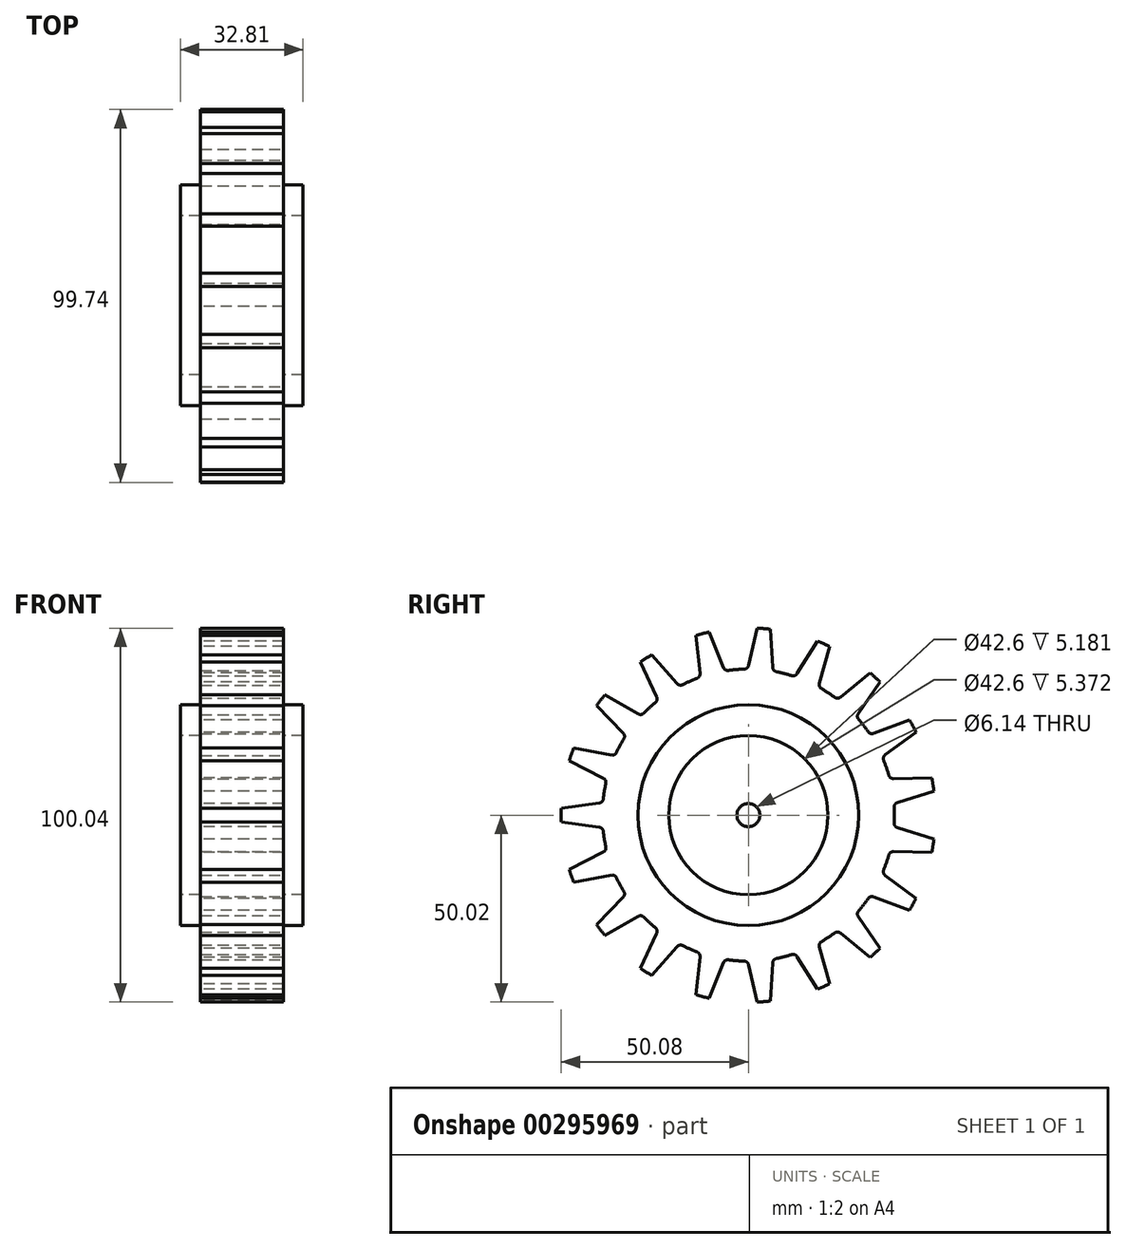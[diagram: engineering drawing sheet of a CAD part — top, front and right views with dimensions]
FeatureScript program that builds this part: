
annotation { "Feature Type Name" : "Feature", "Feature Type Description" : "" }
export const myFeature = defineFeature(function(context is Context, id is Id, definition is map)
    precondition{}
    {
        {
            var Q0;
            Q0=qCreatedBy(makeId("Top.planeOp"),FACE);
            var sketch = newSketch(context, id + "F0", { "sketchPlane" : qUnion([Q0])});
            skLineSegment(sketch, "E0.top", {"start": v(-11.7, 3.07) * mm, "end": v(10.55, 3.07) * mm});
            skLineSegment(sketch, "E0.left", {"start": v(-11.7, 21.68) * mm, "end": v(-11.7, 3.07) * mm});
            skLineSegment(sketch, "E0.right", {"start": v(10.55, 21.68) * mm, "end": v(10.55, 3.07) * mm});
            skLineSegment(sketch, "E1.bottom", {"start": v(-17.08, 29.55) * mm, "end": v(-11.7, 29.55) * mm});
            skLineSegment(sketch, "E1.top", {"start": v(-17.08, 21.3) * mm, "end": v(-11.7, 21.3) * mm});
            skLineSegment(sketch, "E1.left", {"start": v(-17.08, 29.55) * mm, "end": v(-17.08, 21.3) * mm});
            skLineSegment(sketch, "E1.right", {"start": v(15.73, 29.55) * mm, "end": v(15.73, 21.3) * mm});
            skLineSegment(sketch, "E2.top", {"start": v(-11.7, 50.08) * mm, "end": v(10.55, 50.08) * mm});
            skLineSegment(sketch, "E2.left", {"start": v(-11.7, 29.55) * mm, "end": v(-11.7, 50.08) * mm});
            skLineSegment(sketch, "E2.right", {"start": v(10.55, 29.55) * mm, "end": v(10.55, 50.08) * mm});
            skLineSegment(sketch, "E3.trimOffspring", {"start": v(10.55, 21.3) * mm, "end": v(15.73, 21.3) * mm});
            skLineSegment(sketch, "E4.trimOffspring", {"start": v(10.55, 29.55) * mm, "end": v(15.73, 29.55) * mm});
            skLineSegment(sketch, "E5", {"start": v(-71.95, 0) * mm, "end": v(52.19, 0) * mm, "construction": true});
            skLineSegment(sketch, "E6", {"start": v(-0.58, 50.08) * mm, "end": v(0, 0) * mm, "construction": true});
            skSolve(sketch);
        }
        {
            var Q0;
            {var subQ1=sQuery(id+"F0.wireOp",EDGE,"E0.top");Q0=makeQuery(id+"F0.imprint","IMPRINT",FACE,{"disambiguationData":[TD([[makeQuery(id+"F0.imprint","IMPRINT",EDGE,{"derivedFrom":subQ1}),1.0]])]});}
            var Q1;
            Q1=sQuery(id+"F0.wireOp",EDGE,"E5");
            revolve(context, id + "F1", {"entities" : qUnion([Q0]), "axis" : qUnion([Q1]), "revolveType" : RevolveType.FULL});
        }
        {
            var Q0;
            Q0=qCreatedBy(makeId("Right.planeOp"),FACE);
            var sketch = newSketch(context, id + "F2", { "sketchPlane" : qUnion([Q0])});
            skLineSegment(sketch, "E7", {"start": v(49.89, 6.52) * mm, "end": v(38.95, 3.07) * mm});
            skLineSegment(sketch, "E8.MirrorCS", {"start": v(49.89, -6.52) * mm, "end": v(38.95, -3.07) * mm});
            skArc(sketch, "E9", {"start": v(38.95, -3.07) * mm, "mid": v(39.07, 0) * mm, "end": v(38.95, 3.07) * mm});
            skArc(sketch, "E10", {"start": v(49.89, -6.52) * mm, "mid": v(50.31, 0) * mm, "end": v(49.89, 6.52) * mm});
            skSolve(sketch);
        }
        {
            var Q0;
            Q0 = qSketchRegion(id + "F2", true);
            extrude(context, id + "F3", {"entities" : qUnion([Q0]), "operationType" : NewBodyOperationType.REMOVE, "endBound" : BoundingType.SYMMETRIC, "oppositeDirection" : true, "depth" : 152.4 * mm});
        }
        {
            var Q0;
            Q0=makeQuery(id+"F3.boolean.opBoolean","COPY",EDGE,{"derivedFrom":makeQuery(id+"F3.opExtrude","SWEPT_EDGE",EDGE,{"disambiguationData":[OSD([sQuery(id+"F2.wireOp",EDGE,"E7"),sQuery(id+"F2.wireOp",EDGE,"E9")])]})});
            var Q1;
            Q1=makeQuery(id+"F3.boolean.opBoolean","COPY",EDGE,{"derivedFrom":makeQuery(id+"F3.opExtrude","SWEPT_EDGE",EDGE,{"disambiguationData":[OSD([sQuery(id+"F2.wireOp",EDGE,"E8.MirrorCS"),sQuery(id+"F2.wireOp",EDGE,"E9")])]})});
            fillet(context, id + "F4", {"entities" : qUnion([Q0, Q1]), "radius" : 1.27 * mm, "tangentPropagation" : true, "allowEdgeOverflow" : false});
        }
        {
            var Q0;
            Q0=makeQuery(id+"F3.boolean.opBoolean","COPY",FACE,{"derivedFrom":makeQuery(id+"F3.opExtrude","SWEPT_FACE",FACE,{"disambiguationData":[OSD([sQuery(id+"F2.wireOp",EDGE,"E7")])]})});
            var Q1;
            Q1=makeQuery(id+"F3.boolean.opBoolean","COPY",FACE,{"derivedFrom":makeQuery(id+"F3.opExtrude","SWEPT_FACE",FACE,{"disambiguationData":[OSD([sQuery(id+"F2.wireOp",EDGE,"E9")])]})});
            var Q2;
            Q2=makeQuery(id+"F4.opFillet","BLEND_FACE",FACE,{"disambiguationData":[OSD([sQuery(id+"F2.wireOp",EDGE,"E7"),sQuery(id+"F2.wireOp",EDGE,"E9")])]});
            var Q3;
            Q3=makeQuery(id+"F4.opFillet","BLEND_FACE",FACE,{"disambiguationData":[OSD([sQuery(id+"F2.wireOp",EDGE,"E8.MirrorCS"),sQuery(id+"F2.wireOp",EDGE,"E9")])]});
            var Q4;
            Q4=makeQuery(id+"F3.boolean.opBoolean","COPY",FACE,{"derivedFrom":makeQuery(id+"F3.opExtrude","SWEPT_FACE",FACE,{"disambiguationData":[OSD([sQuery(id+"F2.wireOp",EDGE,"E8.MirrorCS")])]})});
            var Q5;
            Q5=sQuery(id+"F0.wireOp",EDGE,"E5");
            circularPattern(context, id + "F5", {"patternType" : PatternType.FACE, "faces" : qUnion([Q0, Q1, Q2, Q3, Q4]), "axis" : qUnion([Q5]), "angle" : 360 * degree, "instanceCount" : 19, "equalSpace" : true});
        }
    });
